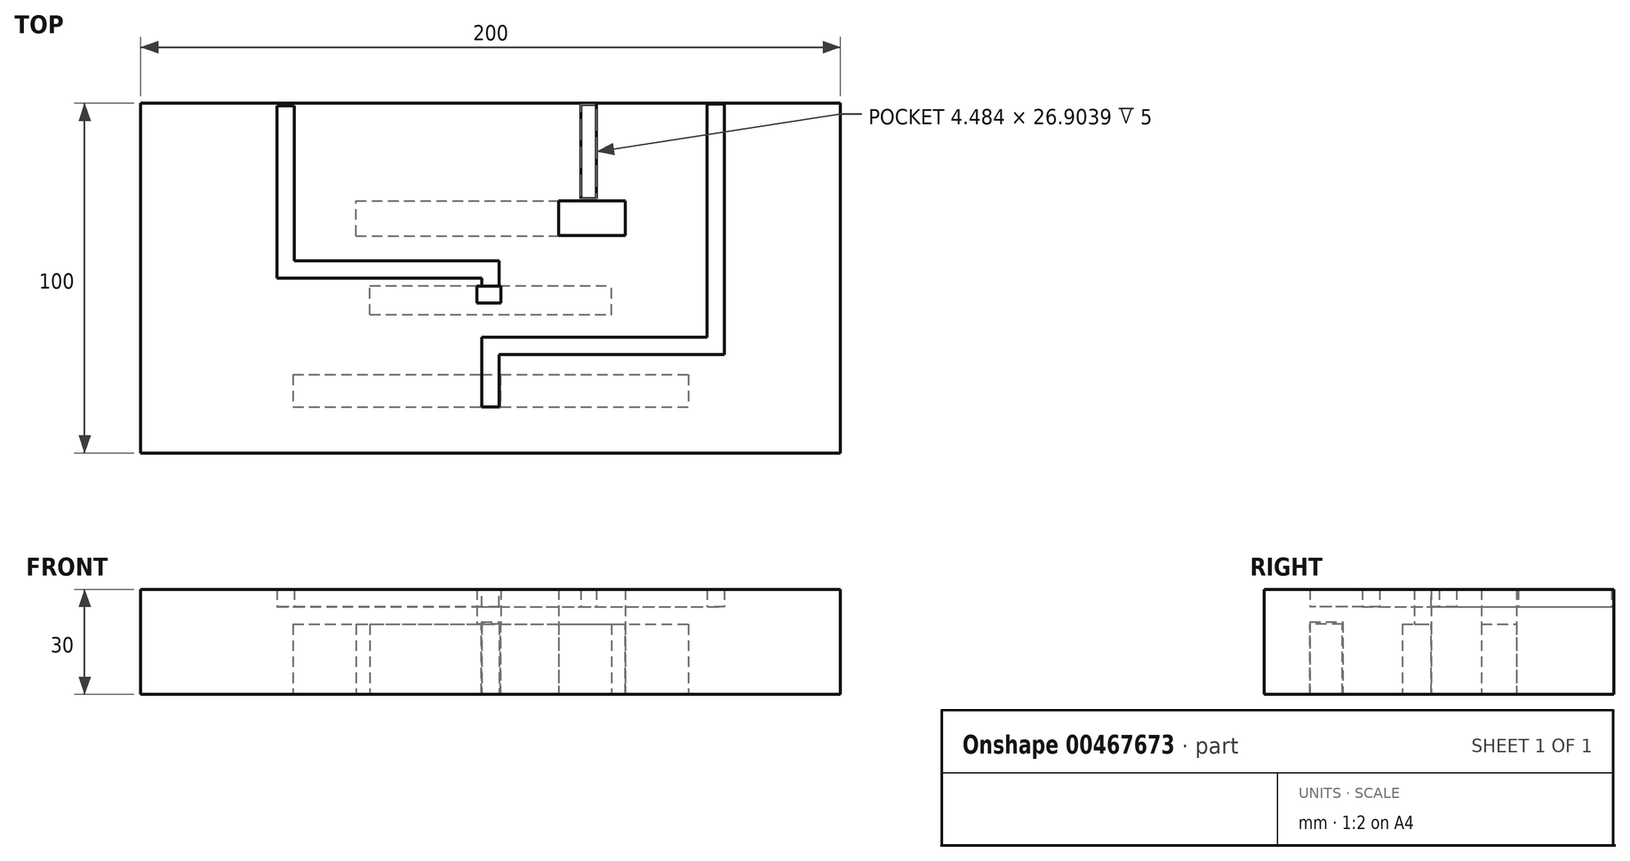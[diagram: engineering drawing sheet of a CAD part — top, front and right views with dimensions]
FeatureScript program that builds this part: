
annotation { "Feature Type Name" : "Feature", "Feature Type Description" : "" }
export const myFeature = defineFeature(function(context is Context, id is Id, definition is map)
    precondition{}
    {
        {
            var Q0;
            Q0=qCreatedBy(makeId("Top.planeOp"),FACE);
            var sketch = newSketch(context, id + "F0", { "sketchPlane" : qUnion([Q0])});
            skLineSegment(sketch, "E0.bottom", {"start": v(-100, 50) * mm, "end": v(100, 50) * mm});
            skLineSegment(sketch, "E0.top", {"start": v(-100, -50) * mm, "end": v(100, -50) * mm});
            skLineSegment(sketch, "E0.left", {"start": v(-100, 50) * mm, "end": v(-100, -50) * mm});
            skLineSegment(sketch, "E0.right", {"start": v(100, 50) * mm, "end": v(100, -50) * mm});
            skPoint(sketch, "E0.middle", {"position": v(0, 0) * mm});
            skSolve(sketch);
        }
        {
            var Q0;
            Q0=makeQuery(id+"F0.imprint","IMPRINT",FACE,{"disambiguationData":[TD([[makeQuery(id+"F0.imprint","IMPRINT",EDGE,{"derivedFrom":sQuery(id+"F0.wireOp",EDGE,"E0.bottom")}),-1.0]])]});
            extrude(context, id + "F1", {"entities" : qUnion([Q0]), "depth" : 30 * mm});
        }
        {
            var Q0;
            Q0=qCreatedBy(makeId("Top.planeOp"),FACE);
            var sketch = newSketch(context, id + "F2", { "sketchPlane" : qUnion([Q0])});
            skLineSegment(sketch, "E1.bottom", {"start": v(-56.5, -27.62) * mm, "end": v(56.5, -27.62) * mm});
            skLineSegment(sketch, "E1.top", {"start": v(-56.5, -36.87) * mm, "end": v(56.5, -36.87) * mm});
            skLineSegment(sketch, "E1.left", {"start": v(-56.5, -27.62) * mm, "end": v(-56.5, -36.87) * mm});
            skLineSegment(sketch, "E1.right", {"start": v(56.5, -27.62) * mm, "end": v(56.5, -36.87) * mm});
            skPoint(sketch, "E1.middle", {"position": v(0, -32.24) * mm});
            skLineSegment(sketch, "E2.bottom", {"start": v(-7, -27.62) * mm, "end": v(7, -27.62) * mm});
            skLineSegment(sketch, "E2.top", {"start": v(-7, -36.87) * mm, "end": v(7, -36.87) * mm});
            skLineSegment(sketch, "E2.left", {"start": v(-7, -27.62) * mm, "end": v(-7, -36.87) * mm});
            skLineSegment(sketch, "E2.right", {"start": v(7, -27.62) * mm, "end": v(7, -36.87) * mm});
            skSolve(sketch);
        }
        {
            var Q0;
            Q0 = qSketchRegion(id + "F2", true);
            extrude(context, id + "F3", {"entities" : qUnion([Q0]), "operationType" : NewBodyOperationType.REMOVE, "depth" : 20 * mm});
        }
        {
            var Q0;
            Q0=qCreatedBy(makeId("Top.planeOp"),FACE);
            var sketch = newSketch(context, id + "F4", { "sketchPlane" : qUnion([Q0])});
            skLineSegment(sketch, "E3.bottom", {"start": v(-34.5, -10.46) * mm, "end": v(34.5, -10.46) * mm});
            skLineSegment(sketch, "E3.top", {"start": v(-34.5, -2.21) * mm, "end": v(34.5, -2.21) * mm});
            skLineSegment(sketch, "E3.left", {"start": v(-34.5, -10.46) * mm, "end": v(-34.5, -2.21) * mm});
            skLineSegment(sketch, "E3.right", {"start": v(34.5, -10.46) * mm, "end": v(34.5, -2.21) * mm});
            skPoint(sketch, "E3.middle", {"position": v(0, -6.34) * mm});
            skSolve(sketch);
        }
        {
            var Q0;
            Q0 = qSketchRegion(id + "F4", true);
            var Q1;
            Q1 = qSketchRegion(id + "F2", true);
            extrude(context, id + "F5", {"entities" : qUnion([Q0, Q1]), "operationType" : NewBodyOperationType.REMOVE, "depth" : 20 * mm});
        }
        {
            var Q0;
            Q0=qCreatedBy(makeId("Top.planeOp"),FACE);
            var sketch = newSketch(context, id + "F6", { "sketchPlane" : qUnion([Q0])});
            skLineSegment(sketch, "E4.bottom", {"start": v(-38.5, 12.11) * mm, "end": v(38.5, 12.11) * mm});
            skLineSegment(sketch, "E4.top", {"start": v(-38.5, 22.11) * mm, "end": v(38.5, 22.11) * mm});
            skLineSegment(sketch, "E4.left", {"start": v(-38.5, 12.11) * mm, "end": v(-38.5, 22.11) * mm});
            skLineSegment(sketch, "E4.right", {"start": v(38.5, 12.11) * mm, "end": v(38.5, 22.11) * mm});
            skPoint(sketch, "E4.middle", {"position": v(0, 17.11) * mm});
            skSolve(sketch);
        }
        {
            var Q0;
            Q0 = qSketchRegion(id + "F6", true);
            extrude(context, id + "F7", {"entities" : qUnion([Q0]), "operationType" : NewBodyOperationType.REMOVE, "depth" : 20 * mm});
        }
        {
            var Q0;
            Q0=qCreatedBy(makeId("Top.planeOp"),FACE);
            var sketch = newSketch(context, id + "F8", { "sketchPlane" : qUnion([Q0])});
            skLineSegment(sketch, "E5.bottom", {"start": v(38.5, 22.12) * mm, "end": v(19.5, 22.12) * mm});
            skLineSegment(sketch, "E5.top", {"start": v(38.5, 12.12) * mm, "end": v(19.5, 12.12) * mm});
            skLineSegment(sketch, "E5.left", {"start": v(38.5, 22.12) * mm, "end": v(38.5, 12.12) * mm});
            skLineSegment(sketch, "E5.right", {"start": v(19.5, 22.12) * mm, "end": v(19.5, 12.12) * mm});
            skSolve(sketch);
        }
        {
            var Q0;
            Q0=makeQuery(id+"F8.imprint","IMPRINT",FACE,{"disambiguationData":[TD([[makeQuery(id+"F8.imprint","IMPRINT",EDGE,{"derivedFrom":sQuery(id+"F8.wireOp",EDGE,"E5.bottom")}),1.0]])]});
            extrude(context, id + "F9", {"entities" : qUnion([Q0]), "operationType" : NewBodyOperationType.REMOVE, "depth" : 40 * mm});
        }
        {
            var Q0;
            Q0=qCreatedBy(makeId("Top.planeOp"),FACE);
            var sketch = newSketch(context, id + "F10", { "sketchPlane" : qUnion([Q0])});
            skLineSegment(sketch, "E6.bottom", {"start": v(25.78, 22.7) * mm, "end": v(30.27, 22.7) * mm});
            skLineSegment(sketch, "E6.top", {"start": v(25.78, 49.6) * mm, "end": v(30.27, 49.6) * mm});
            skLineSegment(sketch, "E6.left", {"start": v(25.78, 22.7) * mm, "end": v(25.78, 49.6) * mm});
            skLineSegment(sketch, "E6.right", {"start": v(30.27, 22.7) * mm, "end": v(30.27, 49.6) * mm});
            skSolve(sketch);
        }
        {
            var Q0;
            Q0 = qSketchRegion(id + "F10", true);
            extrude(context, id + "F11", {"entities" : qUnion([Q0]), "operationType" : NewBodyOperationType.REMOVE, "depth" : 30 * mm});
        }
        {
            var Q0;
            Q0 = qSketchRegion(id + "F10", true);
            extrude(context, id + "F12", {"entities" : qUnion([Q0]), "operationType" : NewBodyOperationType.ADD, "depth" : 25 * mm});
        }
        {
            var Q0;
            Q0=qCreatedBy(makeId("Top.planeOp"),FACE);
            var sketch = newSketch(context, id + "F13", { "sketchPlane" : qUnion([Q0])});
            skLineSegment(sketch, "E7.bottom", {"start": v(-2.5, 5) * mm, "end": v(2.5, 5) * mm});
            skLineSegment(sketch, "E7.top", {"start": v(-2.5, -7.08) * mm, "end": v(2.5, -7.08) * mm});
            skLineSegment(sketch, "E7.left", {"start": v(-2.5, 5) * mm, "end": v(-2.5, -7.08) * mm});
            skLineSegment(sketch, "E7.right", {"start": v(2.5, 5) * mm, "end": v(2.5, -7.08) * mm});
            skPoint(sketch, "E7.middle", {"position": v(0, -1.04) * mm});
            skLineSegment(sketch, "E8.bottom", {"start": v(-2.5, 5) * mm, "end": v(-61.1, 5) * mm});
            skLineSegment(sketch, "E8.top", {"start": v(-2.5, 0) * mm, "end": v(-61.1, 0) * mm});
            skLineSegment(sketch, "E8.left", {"start": v(-2.5, 5) * mm, "end": v(-2.5, 0) * mm});
            skLineSegment(sketch, "E8.right", {"start": v(-61.1, 5) * mm, "end": v(-61.1, 0) * mm});
            skLineSegment(sketch, "E9.bottom", {"start": v(-61.1, 5) * mm, "end": v(-56.1, 5) * mm});
            skLineSegment(sketch, "E9.top", {"start": v(-61.1, 49.27) * mm, "end": v(-56.1, 49.27) * mm});
            skLineSegment(sketch, "E9.left", {"start": v(-61.1, 5) * mm, "end": v(-61.1, 49.27) * mm});
            skLineSegment(sketch, "E9.right", {"start": v(-56.1, 5) * mm, "end": v(-56.1, 49.27) * mm});
            skSolve(sketch);
        }
        {
            var Q0;
            Q0 = qSketchRegion(id + "F13", true);
            extrude(context, id + "F14", {"entities" : qUnion([Q0]), "operationType" : NewBodyOperationType.REMOVE, "depth" : 30 * mm});
        }
        {
            var Q0;
            Q0 = qSketchRegion(id + "F13", true);
            extrude(context, id + "F15", {"entities" : qUnion([Q0]), "operationType" : NewBodyOperationType.ADD, "depth" : 25 * mm});
        }
        {
            var Q0;
            Q0=qCreatedBy(makeId("Top.planeOp"),FACE);
            var sketch = newSketch(context, id + "F16", { "sketchPlane" : qUnion([Q0])});
            skLineSegment(sketch, "E10.bottom", {"start": v(-2.5, -21.9) * mm, "end": v(2.5, -21.9) * mm});
            skLineSegment(sketch, "E10.top", {"start": v(-2.5, -36.9) * mm, "end": v(2.5, -36.9) * mm});
            skLineSegment(sketch, "E10.left", {"start": v(-2.5, -21.9) * mm, "end": v(-2.5, -36.9) * mm});
            skLineSegment(sketch, "E10.right", {"start": v(2.5, -21.9) * mm, "end": v(2.5, -36.9) * mm});
            skPoint(sketch, "E10.middle", {"position": v(0, -29.4) * mm});
            skLineSegment(sketch, "E11.bottom", {"start": v(-2.5, -21.9) * mm, "end": v(66.86, -21.9) * mm});
            skLineSegment(sketch, "E11.top", {"start": v(-2.5, -16.9) * mm, "end": v(66.86, -16.9) * mm});
            skLineSegment(sketch, "E11.left", {"start": v(-2.5, -21.9) * mm, "end": v(-2.5, -16.9) * mm});
            skLineSegment(sketch, "E11.right", {"start": v(66.86, -21.9) * mm, "end": v(66.86, -16.9) * mm});
            skLineSegment(sketch, "E12.bottom", {"start": v(66.86, -16.9) * mm, "end": v(61.86, -16.9) * mm});
            skLineSegment(sketch, "E12.top", {"start": v(66.86, 49.71) * mm, "end": v(61.86, 49.71) * mm});
            skLineSegment(sketch, "E12.left", {"start": v(66.86, -16.9) * mm, "end": v(66.86, 49.71) * mm});
            skLineSegment(sketch, "E12.right", {"start": v(61.86, -16.9) * mm, "end": v(61.86, 49.71) * mm});
            skSolve(sketch);
        }
        {
            var Q0;
            Q0 = qSketchRegion(id + "F16", true);
            extrude(context, id + "F17", {"entities" : qUnion([Q0]), "operationType" : NewBodyOperationType.REMOVE, "depth" : 30 * mm});
        }
        {
            var Q0;
            Q0 = qSketchRegion(id + "F16", true);
            extrude(context, id + "F18", {"entities" : qUnion([Q0]), "operationType" : NewBodyOperationType.ADD, "depth" : 25 * mm});
        }
        {
            var Q0;
            Q0=qCreatedBy(makeId("Top.planeOp"),FACE);
            var sketch = newSketch(context, id + "F19", { "sketchPlane" : qUnion([Q0])});
            skLineSegment(sketch, "E13.bottom", {"start": v(-2.59, -36.92) * mm, "end": v(2.86, -36.92) * mm});
            skLineSegment(sketch, "E13.top", {"start": v(-2.59, -27.56) * mm, "end": v(2.86, -27.56) * mm});
            skLineSegment(sketch, "E13.left", {"start": v(-2.59, -36.92) * mm, "end": v(-2.59, -27.56) * mm});
            skLineSegment(sketch, "E13.right", {"start": v(2.86, -36.92) * mm, "end": v(2.86, -27.56) * mm});
            skSolve(sketch);
        }
        {
            var Q0;
            Q0 = qSketchRegion(id + "F19", true);
            extrude(context, id + "F20", {"entities" : qUnion([Q0]), "operationType" : NewBodyOperationType.REMOVE, "oppositeDirection" : true, "depth" : 30 * mm});
        }
        {
            var Q0;
            Q0 = qSketchRegion(id + "F19", true);
            extrude(context, id + "F21", {"entities" : qUnion([Q0]), "operationType" : NewBodyOperationType.REMOVE, "endBound" : BoundingType.THROUGH_ALL, "oppositeDirection" : true, "depth" : 25 * mm});
        }
        {
            var Q0;
            Q0 = qSketchRegion(id + "F19", true);
            extrude(context, id + "F22", {"entities" : qUnion([Q0]), "operationType" : NewBodyOperationType.REMOVE, "oppositeDirection" : true, "depth" : 37.7 * mm});
        }
        {
            var Q0;
            Q0 = qSketchRegion(id + "F19", true);
            extrude(context, id + "F23", {"entities" : qUnion([Q0]), "operationType" : NewBodyOperationType.REMOVE, "depth" : 20.7 * mm});
        }
        {
            var Q0;
            Q0=qCreatedBy(makeId("Top.planeOp"),FACE);
            var sketch = newSketch(context, id + "F24", { "sketchPlane" : qUnion([Q0])});
            skLineSegment(sketch, "E14.bottom", {"start": v(-3.94, -2.27) * mm, "end": v(2.97, -2.27) * mm});
            skLineSegment(sketch, "E14.top", {"start": v(-3.94, -7.11) * mm, "end": v(2.97, -7.11) * mm});
            skLineSegment(sketch, "E14.left", {"start": v(-3.94, -2.27) * mm, "end": v(-3.94, -7.11) * mm});
            skLineSegment(sketch, "E14.right", {"start": v(2.97, -2.27) * mm, "end": v(2.97, -7.11) * mm});
            skSolve(sketch);
        }
        {
            var Q0;
            Q0 = qSketchRegion(id + "F24", true);
            extrude(context, id + "F25", {"entities" : qUnion([Q0]), "operationType" : NewBodyOperationType.REMOVE, "depth" : 32.6 * mm});
        }
    });
